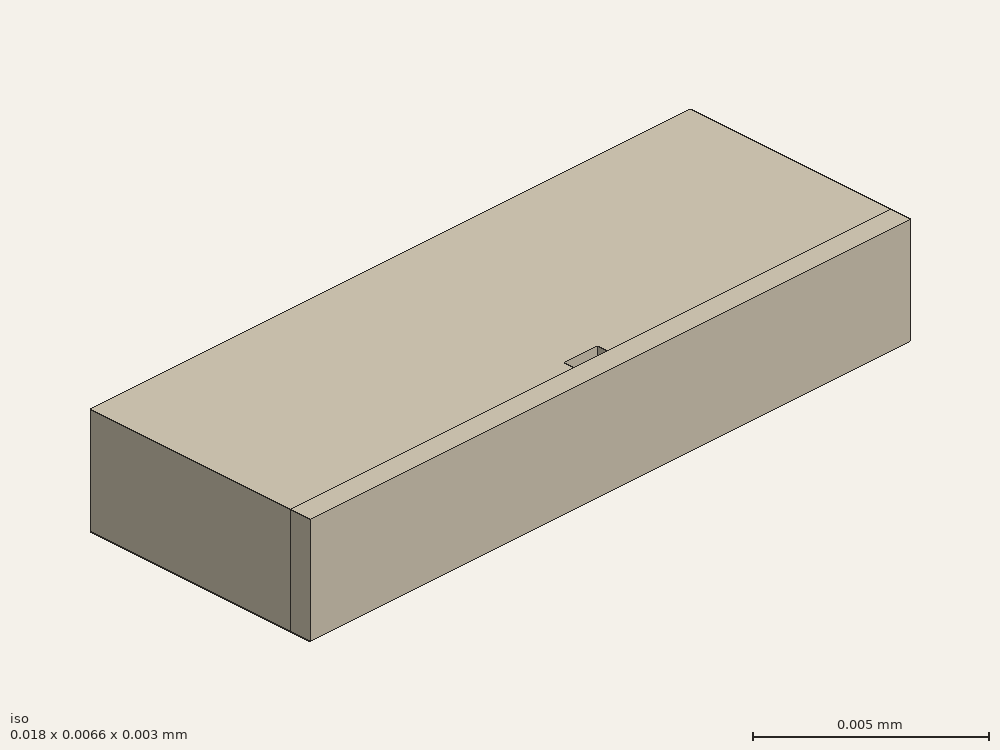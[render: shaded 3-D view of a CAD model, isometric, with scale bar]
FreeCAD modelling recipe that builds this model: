
FCSTD DOCUMENT  (FreeCAD 0.21R33694 (Git))
Label: strip
License: All rights reserved
LicenseURL: http://en.wikipedia.org/wiki/All_rights_reserved
objects: Part::Part2DObjectPython×9, App::FeaturePython×6, Part::Extrusion×3, Part::Cut×1, Part::FeaturePython×1
note: 14 computed .brp shape members not serialized (recipe doc carries the construction recipe); baked Part::Feature solids carry a one-line shape summary decoded from their .brp

FEATURE [Part::Part2DObjectPython] Rectangle  # Draft 2D object (typed FeaturePython)
  Area = 1.143e-05
  ChamferSize = 0
  Columns = 1
  FilletRadius = 0
  Height = 0.000635
  Length = 0.018
  MakeFace = true
  Placement = pos=(-0.009,0,0) rot=(0,0,1;0rad)
  Rows = 1
FEATURE [Part::Part2DObjectPython] Rectangle001  # Draft 2D object (typed FeaturePython)
  Area = 0.000108
  ChamferSize = 0
  Columns = 1
  FilletRadius = 0
  Height = 0.006
  Length = 0.018
  MakeFace = true
  Placement = pos=(-0.009,0.000635,0) rot=(0,0,1;0rad)
  Rows = 1
FEATURE [Part::Part2DObjectPython] Rectangle002  # Draft 2D object (typed FeaturePython)
  Area = 3e-07
  ChamferSize = 0
  Columns = 1
  FilletRadius = 0
  Height = 0.0003
  Length = 0.001
  MakeFace = true
  Placement = pos=(-0.0005,0.000635,0) rot=(0,0,1;0rad)
  Rows = 1
FEATURE [Part::Extrusion] Extrude  label="substrate1"
  Base = -> Rectangle
  Dir = (0,0,1)
  DirMode = 2
  FaceMakerClass = Part::FaceMakerBullseye
  LengthFwd = 0.003
  LengthRev = 0
  Solid = false
  Symmetric = false
FEATURE [Part::Extrusion] Extrude001
  Base = -> Rectangle002
  Dir = (0,0,1)
  DirMode = 2
  FaceMakerClass = Part::FaceMakerBullseye
  LengthFwd = 0.003
  LengthRev = 0
  Solid = false
  Symmetric = false
FEATURE [Part::Extrusion] Extrude002
  Base = -> Rectangle001
  Dir = (0,0,1)
  DirMode = 2
  FaceMakerClass = Part::FaceMakerBullseye
  LengthFwd = 0.003
  LengthRev = 0
  Solid = false
  Symmetric = false
FEATURE [Part::Cut] Cut  label="air1"
  Base = -> Extrude002
  Tool = -> Extrude001
FEATURE [Part::Part2DObjectPython] Rectangle003  label="_Pport1"  # Draft 2D object (typed FeaturePython)
  Area = 0.00011943
  ChamferSize = 0
  Columns = 1
  FilletRadius = 0
  Height = 0.006635
  Length = 0.018
  MakeFace = true
  Placement = pos=(-0.009,0,0.003) rot=(0,0,1;0rad)
  Rows = 1
FEATURE [Part::Part2DObjectPython] Rectangle004  label="_Pi1"  # Draft 2D object (typed FeaturePython)
  Area = 3e-07
  ChamferSize = 0
  Columns = 1
  FilletRadius = 0
  Height = 0.0003
  Length = 0.001
  MakeFace = true
  Placement = pos=(-0.0005,0.000635,0.003) rot=(0,0,1;0rad)
  Rows = 1
FEATURE [Part::Part2DObjectPython] Line  label="_Pv1"  # Draft 2D object (typed FeaturePython)
  Area = 0
  ChamferSize = 0
  Closed = false
  End = (0,0.000635,0.003)
  FilletRadius = 0
  Length = 0.000635
  MakeFace = true
  Placement = pos=(0,0,0.003) rot=(0,0,1;0rad)
  Points = (2) [(0,0,0),(3.88825e-20,0.000635,0)]
  Start = (0,0,0.003)
  Subdivisions = 0
FEATURE [Part::Part2DObjectPython] Rectangle005  label="_Pport2"  # Draft 2D object (typed FeaturePython)
  Area = 0.00011943
  ChamferSize = 0
  Columns = 1
  FilletRadius = 0
  Height = 0.006635
  Length = 0.018
  MakeFace = true
  Placement = pos=(-0.009,0,0) rot=(0,0,1;0rad)
  Rows = 1
FEATURE [Part::Part2DObjectPython] Rectangle006  label="_Pi2"  # Draft 2D object (typed FeaturePython)
  Area = 3e-07
  ChamferSize = 0
  Columns = 1
  FilletRadius = 0
  Height = 0.0003
  Length = 0.001
  MakeFace = true
  Placement = pos=(-0.0005,0.000635,0) rot=(0,0,1;0rad)
  Rows = 1
FEATURE [Part::Part2DObjectPython] Line001  label="_Pv2"  # Draft 2D object (typed FeaturePython)
  Area = 0
  ChamferSize = 0
  Closed = false
  End = (0,0.000635,0)
  FilletRadius = 0
  Length = 0.000635
  MakeFace = true
  Points = (2) [(0,0,0),(1.77361e-18,0.000635,0)]
  Start = (0,0,0)
  Subdivisions = 0
FEATURE [App::FeaturePython] Text  label="_S1(PV){port1}"  # WARN: FeaturePython — macro-defined, semantics opaque (R4)
  Placement = pos=(-0.0005,0.00209073,-0.00864056) rot=(0.57735,0.57735,0.57735;2.0944rad)
  Text = .
FEATURE [App::FeaturePython] Text001  label="_S2(PV){port2}"  # WARN: FeaturePython — macro-defined, semantics opaque (R4)
  Placement = pos=(-0.0005,0.00209073,-0.00864056) rot=(0.57735,0.57735,0.57735;2.0944rad)
  Text = .
FEATURE [App::FeaturePython] Text002  label="_L1(1,voltage){v1}"  # WARN: FeaturePython — macro-defined, semantics opaque (R4)
  Placement = pos=(-0.0005,0.00209073,-0.00864056) rot=(0.57735,0.57735,0.57735;2.0944rad)
  Text = .
FEATURE [App::FeaturePython] Text003  label="_L1(1,current){i1}"  # WARN: FeaturePython — macro-defined, semantics opaque (R4)
  Placement = pos=(-0.0005,0.00209073,-0.00864056) rot=(0.57735,0.57735,0.57735;2.0944rad)
  Text = .
FEATURE [App::FeaturePython] Text004  label="_L2(2,voltage){v2}"  # WARN: FeaturePython — macro-defined, semantics opaque (R4)
  Placement = pos=(-0.0005,0.00209073,-0.00864056) rot=(0.57735,0.57735,0.57735;2.0944rad)
  Text = .
FEATURE [App::FeaturePython] Text005  label="_L2(2,current){i2}"  # WARN: FeaturePython — macro-defined, semantics opaque (R4)
  Placement = pos=(-0.0005,0.00209073,-0.00864056) rot=(0.57735,0.57735,0.57735;2.0944rad)
  Text = .
FEATURE [Part::FeaturePython] BooleanFragments  # WARN: FeaturePython — macro-defined, semantics opaque (R4)
  Mode = 0
  Objects = -> [Extrude,Cut]
  Tolerance = 0
